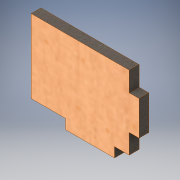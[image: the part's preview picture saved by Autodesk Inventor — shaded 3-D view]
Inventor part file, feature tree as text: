
AUTODESK INVENTOR PART (.ipt)
format: ipt  version: 2019 (Build 230136000, 136)  size: 128,512 bytes
history: native  units: mm
features: other x1, extrude x1, sketch x1
ambient origin geometry x8: Origin, YZ Plane, XZ Plane, XY Plane, X Axis, Y Axis, Z Axis, Center Point
bodies: Body1 (feature_tree)
feature tree (3):
  other  "Твердое тело1"
  extrude  "Выдавливание1"  Depth=4.0mm
  sketch  "Эскиз1"
